# Revit family: Grohe_PlumbingFixture_Bauflow_SingleLeverBathMixer_29045000a
name_source: partatom
category: Plumbing Fixtures
revit_build: Autodesk Revit 2018 (Build: 20190510_1515(x64)
units: mm (PartAtom-declared; Revit-internal decimal feet)

## family parameters
Cut with Voids When Loaded = No
Host = Face
OmniClass Number = 23.65.00.00
OmniClass Title = Supply and Distribution of Liquids and Gases
Part Type = Normal
Room Calculation Point = No
Round Connector Dimension = Use Diameter
Shared = No

## types (1)
- 29045000
    ADACompliant = No
    Assembly Code = D2010
    AssetType = Fixed
    BIMObjectName = Grohe_PlumbingFixture_Bauflow_SingleLeverBathMixer_29045000
    CWFU = 0
    ClassificationName = Uniclass 2015
    ClassificationValue = Pr_40_20_87_07
    ColdWaterConnectionDiameter = 10 mm  [stored 0.0328084 ft]
    Color = Chrome
    Cost = 0 $
    Default Elevation = 0 mm  [stored 0 ft]
    Description = Created for contemporary bathrooms where there is a full shower over the bathtub, this GROHE BauFlow single-lever bath mixer will bring flowing, harmonious lines and great performance to your scheme. The wall-mounted, concealed mixer lets you switch effortlessly between the bath and shower. It features an adjustable flow rate limiter with a minimum flow rate of 2.5l/min. Operation is via a solid metal lever handle. This set includes the GROHE concealed body (32963000). Internally the GROHE LongLife ceramic cartridge delivers reliable volume control and durability. And thanks to the sparkling and hardwearing GROHE StarLight chrome finish this bathroom mixer will stay looking immaculate for years to come.
    DocumentationCertificates = www.grohe.co.uk/
    DocumentationInstallationGuide = www.grohe.co.uk/
    DocumentationLiterature = www.grohe.co.uk/
    DocumentationMaintenance = www.grohe.co.uk/
    DocumentationTechnical = www.grohe.co.uk/
    DurationUnit = Years
    Ecojoy = No
    ExpectedLife = 0
    FaucetMaterial = Grohe-Chrome
    Features = concealed installation 
consisting of: 
set for final installation 
concealed body (32 963 001) 
metal lever 
GROHE Longlife 46 mm ceramic cartridge 
GROHE StarLight chrome finish 
adjustable flow rate limiter 
adjustable minimum flow rate approx. 2.5 l/min 
automatic diverter: bath/shower 
escutcheon- and shaft-sealing 
optional temperature limiter
    HWFU = 0
    HotWaterConnectionDiameter = 10 mm  [stored 0.0328084 ft]
    IfcExportAs = IfcPipeFitting
    IfcExportType = IfcPipeFittingType
    Keynote = N13
    LowEmittingMaterial = No
    Manufacturer = Grohe
    ManufacturerName = Grohe
    MasterformatNumber = 01 52 19
    MasterformatTitle = Sanitary Facilities
    Model = BAUFLOW
    ModelNumber = 29045000
    ModelReference = BAUFLOW - SINGLE-LEVER BATH MIXER
    NBSDescription = Water supply fittings for baths
    NBSObjectName = Grohe - Water supply fittings for baths
    NBSReference = 45-35-70/315
    NominalDepth = 0 mm  [stored 0 ft]
    NominalHeight = 0 mm  [stored 0 ft]
    NominalLength = 0 mm  [stored 0 ft]
    ProductPageURL = https://www.grohe.co.in
    ProductionYear = 2020
    Type Comments = SINGLE-LEVER BATH MIXER
    TypeName = BAUFLOW - SINGLE-LEVER BATH MIXER
    URL = www.grohe.com
    WarrantyDurationLabor = 0
    WarrantyDurationParts = 0
    WarrantyDurationUnit = Years
    _BSBibleVersion = 16
    _BimSpecGuid = 0
    _CurrentRevision = 1
    _DistributedBy = www.bimstore.co
    _ObjectUserGuide = www.bimstore.co

note: [stored X ft] marks values corroborated as IEEE doubles in the binary element streams (Revit-internal decimal feet)

## geometry (parser evidence)
native form markers: Sweep x3
no freeform markers — native parametric forms only
